# Revit family: Канальный блок VRF-системы
name_source: partatom
category: Mechanical Equipment
revit_build: Autodesk Revit 2016 (Build: 20150506_1715(x64)
units: mm (PartAtom-declared; Revit-internal decimal feet)

## family parameters
Cut with Voids When Loaded = No
Host = Face
Part Type = Normal
Room Calculation Point = No
Round Connector Dimension = Use Diameter
Shared = No

## types (10) — shared parameters
Default Elevation = 1219.2 mm  [stored 4 ft]
Высота воздуховода = 176 mm  [stored 0.577428 ft]
Наименование = Канальный блок VRF-системы
Производитель = Electrolux
Таблица модель = Модель
Таблица наименование = Наименование
Таблица параметров = Таблица параметров
Таблица расход воздуха = Расход воздуха
Таблица уровень звукового давления = Уровень звукового давления
Таблица электропитание = Электропитание
Фаза = 1
Частота сети = 50 Hz
Эл. питание(коннектор) = 220 V
Электропитание, (В) = 220

## per-type parameters (varying)
| type | Артикул | Вес | Высота | Глубина | Диаметр газовой трубы | Диаметр жидкостной трубы | Расход воздуха, (м.куб/ч) | Теплопроизводительность | Уровень звукового давления, (Дб(А)) | Холодопроизводительность | Ширина | Ширина воздуховода |
| ESVMD-SF-22 | 1022697 | 25.00 kg | 270 mm  [stored 0.885827 ft] | 720 mm  [stored 2.3622 ft] | 12.7 mm  [stored 0.0416667 ft] | 6.35 mm  [stored 0.0208333 ft] | 480-420-360 | 2.80 kW | 33-31-29 | 2.20 kW | 650 mm  [stored 2.13255 ft] | 590 mm  [stored 1.9357 ft] |
| ESVMD-SF-28 | 1022698 | 25.00 kg | 270 mm  [stored 0.885827 ft] | 720 mm  [stored 2.3622 ft] | 12.7 mm  [stored 0.0416667 ft] | 6.35 mm  [stored 0.0208333 ft] | 480-420-360 | 3.30 kW | 33-31-29 | 2.80 kW | 650 mm  [stored 2.13255 ft] | 590 mm  [stored 1.9357 ft] |
| ESVMD-SF-36 | 1022699 | 25.00 kg | 270 mm  [stored 0.885827 ft] | 720 mm  [stored 2.3622 ft] | 12.7 mm  [stored 0.0416667 ft] | 6.35 mm  [stored 0.0208333 ft] | 780-660-540 | 4.20 kW | 33-31-29 | 3.60 kW | 650 mm  [stored 2.13255 ft] | 590 mm  [stored 1.9357 ft] |
| ESVMD-SF-50 | 1022700 | 34.00 kg | 270 mm  [stored 0.885827 ft] | 720 mm  [stored 2.3622 ft] | 15.88 mm  [stored 0.0520997 ft] | 6.35 mm  [stored 0.0208333 ft] | 900-780-660 | 5.60 kW | 34-32-30 | 5.00 kW | 900 mm  [stored 2.95276 ft] | 840 mm  [stored 2.75591 ft] |
| ESVMD-SF-56 | 1022701 | 34.00 kg | 270 mm  [stored 0.885827 ft] | 720 mm  [stored 2.3622 ft] | 15.88 mm  [stored 0.0520997 ft] | 6.35 mm  [stored 0.0208333 ft] | 900-780-660 | 6.50 kW | 34-32-30 | 5.60 kW | 900 mm  [stored 2.95276 ft] | 840 mm  [stored 2.75591 ft] |
| ESVMD-SF-71 | 1022702 | 34.00 kg | 270 mm  [stored 0.885827 ft] | 720 mm  [stored 2.3622 ft] | 15.88 mm  [stored 0.0520997 ft] | 9.53 mm | 960-840-720 | 8.50 kW | 36-34-32 | 7.10 kW | 900 mm  [stored 2.95276 ft] | 840 mm  [stored 2.75591 ft] |
| ESVMD-SF-90 | 1022703 | 44.00 kg | 350 mm  [stored 1.14829 ft] | 800 mm  [stored 2.62467 ft] | 15.88 mm  [stored 0.0520997 ft] | 9.53 mm | 1600-1400-1150 | 10.00 kW | 41-39-34 | 9.00 kW | 900 mm  [stored 2.95276 ft] | 840 mm  [stored 2.75591 ft] |
| ESVMD-SF-112 | 1022704 | 44.00 kg | 350 mm  [stored 1.14829 ft] | 800 mm  [stored 2.62467 ft] | 15.88 mm  [stored 0.0520997 ft] | 9.53 mm | 1600-1400-1150 | 13.00 kW | 43-40-36 | 11.20 kW | 900 mm  [stored 2.95276 ft] | 840 mm  [stored 2.75591 ft] |
| ESVMD-SF-140 | 1022705 | 56.00 kg | 350 mm  [stored 1.14829 ft] | 800 mm  [stored 2.62467 ft] | 15.88 mm  [stored 0.0520997 ft] | 9.53 mm | 2100-1750-1450 | 16.30 kW | 44-41-36 | 14.20 kW | 1300 mm  [stored 4.26509 ft] | 1240 mm |
| ESVMD-SF-160 | 1022706 | 56.00 kg | 350 mm  [stored 1.14829 ft] | 800 mm  [stored 2.62467 ft] | 15.88 mm  [stored 0.0520997 ft] | 9.53 mm | 2150-1900-1620 | 18.00 kW | 43-40-37 | 16.00 kW | 1300 mm  [stored 4.26509 ft] | 1240 mm |

note: column(s) folded — value = type name in every type: Модель

note: [stored X ft] marks values corroborated as IEEE doubles in the binary element streams (Revit-internal decimal feet)
